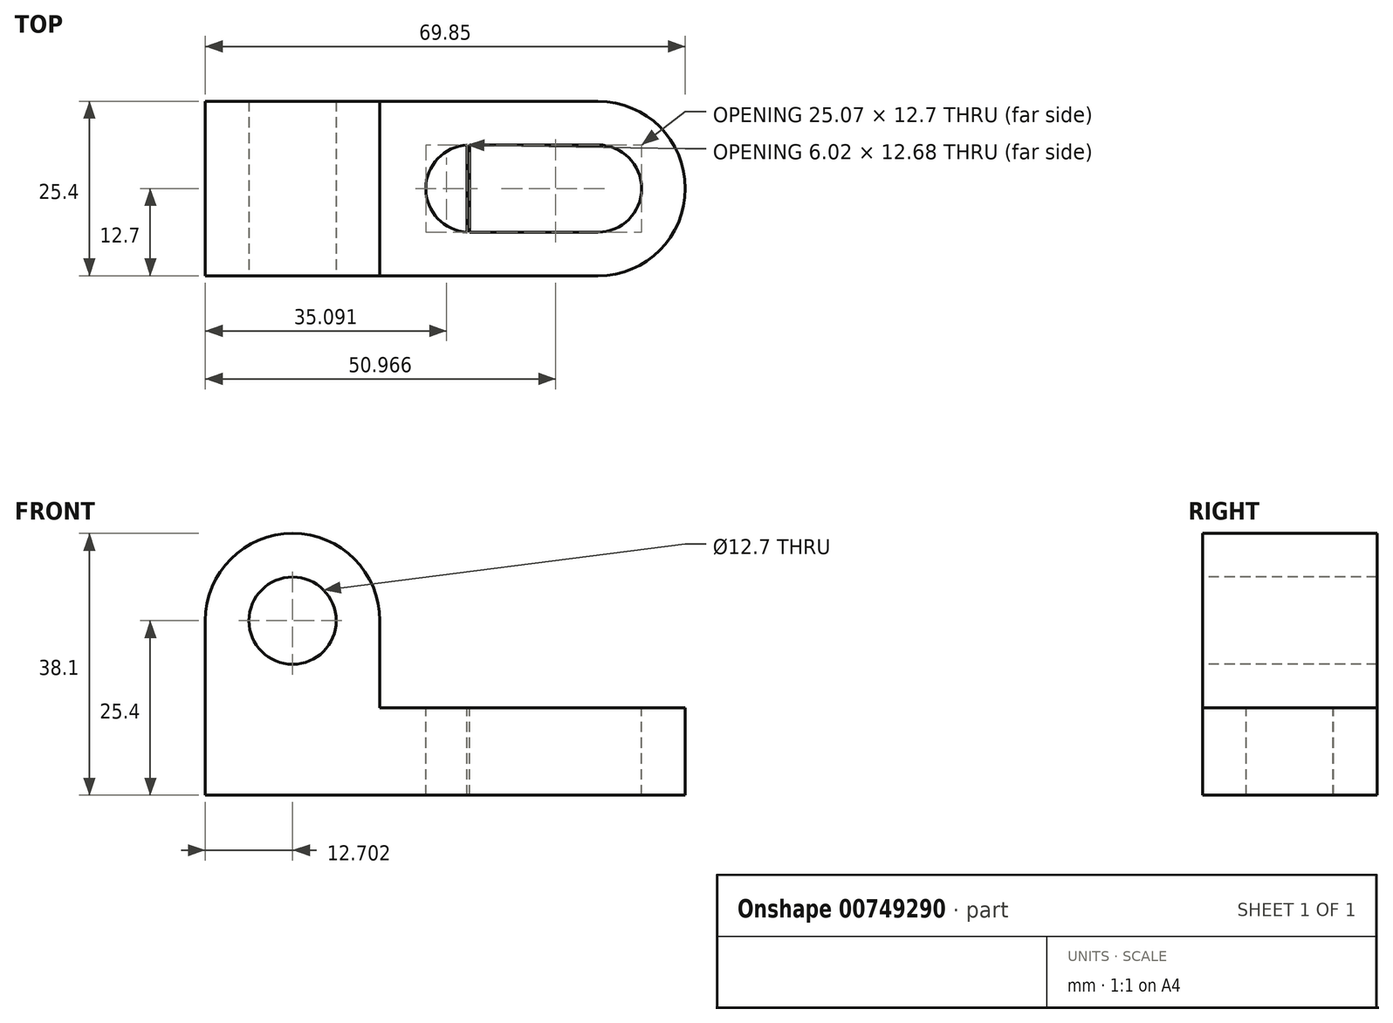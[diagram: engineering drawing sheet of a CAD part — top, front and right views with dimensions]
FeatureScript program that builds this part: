
annotation { "Feature Type Name" : "Feature", "Feature Type Description" : "" }
export const myFeature = defineFeature(function(context is Context, id is Id, definition is map)
    precondition{}
    {
        {
            var Q0;
            Q0=qCreatedBy(makeId("Front.planeOp"),FACE);
            var sketch = newSketch(context, id + "F0", { "sketchPlane" : qUnion([Q0])});
            skLineSegment(sketch, "E0", {"start": v(-38.43, 0) * mm, "end": v(-38.43, 38.1) * mm});
            skLineSegment(sketch, "E1", {"start": v(-38.43, 38.1) * mm, "end": v(-13.03, 38.1) * mm});
            skLineSegment(sketch, "E2", {"start": v(-13.03, 38.1) * mm, "end": v(-13.03, 12.7) * mm});
            skLineSegment(sketch, "E3", {"start": v(-13.03, 12.7) * mm, "end": v(31.42, 12.7) * mm});
            skLineSegment(sketch, "E4", {"start": v(31.42, 12.7) * mm, "end": v(31.42, 0) * mm});
            skLineSegment(sketch, "E5", {"start": v(31.42, 0) * mm, "end": v(-38.43, 0) * mm});
            skSolve(sketch);
        }
        {
            var Q0;
            Q0=makeQuery(id+"F0.imprint","IMPRINT",FACE,{"disambiguationData":[TD([[makeQuery(id+"F0.imprint","IMPRINT",EDGE,{"derivedFrom":sQuery(id+"F0.wireOp",EDGE,"E0")}),-1.0]])]});
            extrude(context, id + "F1", {"entities" : qUnion([Q0]), "depth" : 25.4 * mm, "offsetDistance" : 25.4 * mm});
        }
        {
            var Q0;
            Q0=makeQuery(id+"F1.opExtrude","CAP_FACE",FACE,{"disambiguationData":[OSD([sQuery(id+"F0.wireOp",EDGE,"E0"),sQuery(id+"F0.wireOp",EDGE,"E1"),sQuery(id+"F0.wireOp",EDGE,"E2"),sQuery(id+"F0.wireOp",EDGE,"E3"),sQuery(id+"F0.wireOp",EDGE,"E4"),sQuery(id+"F0.wireOp",EDGE,"E5")])],"isStart":false});
            var sketch = newSketch(context, id + "F2", { "sketchPlane" : qUnion([Q0])});
            skLineSegment(sketch, "E6", {"start": v(-38.43, 25.4) * mm, "end": v(-13.03, 25.4) * mm});
            skLineSegment(sketch, "E7", {"start": v(-13.03, 25.4) * mm, "end": v(-13.03, 38.1) * mm});
            skCircle(sketch, "E8", {"center": v(-25.73, 25.4) * mm, "radius": 6.35 * mm});
            skArc(sketch, "E9", {"start": v(-13.03, 25.4) * mm, "mid": v(-25.73, 38.1) * mm, "end": v(-38.43, 25.4) * mm});
            skSolve(sketch);
        }
        {
            var Q0;
            {var subQ1=makeQuery(id+"F1.opExtrude","CAP_EDGE",EDGE,{"disambiguationData":[OSD([sQuery(id+"F0.wireOp",EDGE,"E0")])],"isStart":false});var subQ3=makeQuery(id+"F1.opExtrude","CAP_EDGE",EDGE,{"disambiguationData":[OSD([sQuery(id+"F0.wireOp",EDGE,"E1")])],"isStart":false});var subQ5=makeQuery(id+"F2.imprint","INTERSECT",VERTEX,{"derivedFrom":[subQ1,subQ3]});Q0=makeQuery(id+"F2.imprint","IMPRINT",FACE,{"disambiguationData":[TD([[makeQuery(id+"F2.imprint","IMPRINT",EDGE,{"disambiguationData":[TD([[subQ5,-1.0]])],"derivedFrom":subQ3}),-1.0]])]});}
            var Q1;
            {var subQ0=sQuery(id+"F2.wireOp",EDGE,"E7");Q1=makeQuery(id+"F2.imprint","IMPRINT",FACE,{"disambiguationData":[TD([[makeQuery(id+"F2.imprint","IMPRINT",EDGE,{"derivedFrom":subQ0}),-1.0]])]});}
            var Q2;
            {var subQ0=sQuery(id+"F2.wireOp",EDGE,"E8");var subQ1=sQuery(id+"F2.wireOp",EDGE,"E6");var subQ2=makeQuery(id+"F2.imprint","INTERSECT",VERTEX,{"disambiguationData":[OD(0.0)],"derivedFrom":[subQ1,subQ0]});Q2=makeQuery(id+"F2.imprint","IMPRINT",FACE,{"disambiguationData":[TD([[makeQuery(id+"F2.imprint","IMPRINT",EDGE,{"disambiguationData":[TD([[subQ2,-1.0]])],"derivedFrom":subQ1}),1.0]])]});}
            var Q3;
            {var subQ0=sQuery(id+"F2.wireOp",EDGE,"E8");var subQ1=sQuery(id+"F2.wireOp",EDGE,"E6");var subQ2=makeQuery(id+"F2.imprint","INTERSECT",VERTEX,{"disambiguationData":[OD(0.0)],"derivedFrom":[subQ1,subQ0]});Q3=makeQuery(id+"F2.imprint","IMPRINT",FACE,{"disambiguationData":[TD([[makeQuery(id+"F2.imprint","IMPRINT",EDGE,{"disambiguationData":[TD([[subQ2,-1.0]])],"derivedFrom":subQ1}),-1.0]])]});}
            extrude(context, id + "F3", {"entities" : qUnion([Q0, Q1, Q2, Q3]), "operationType" : NewBodyOperationType.REMOVE, "endBound" : BoundingType.THROUGH_ALL, "oppositeDirection" : true, "depth" : 25.4 * mm, "offsetDistance" : 25.4 * mm});
        }
        {
            var Q0;
            Q0=makeQuery(id+"F1.opExtrude","SWEPT_FACE",FACE,{"disambiguationData":[OSD([sQuery(id+"F0.wireOp",EDGE,"E3")])]});
            var sketch = newSketch(context, id + "F4", { "sketchPlane" : qUnion([Q0])});
            skLineSegment(sketch, "E10", {"start": v(0, 0) * mm, "end": v(0, -25.4) * mm});
            skLineSegment(sketch, "E11", {"start": v(18.72, 0) * mm, "end": v(18.72, -25.4) * mm});
            skLineSegment(sketch, "E12", {"start": v(18.72, 0) * mm, "end": v(31.42, 0) * mm});
            skLineSegment(sketch, "E13", {"start": v(0, 0) * mm, "end": v(18.72, 0) * mm});
            skLineSegment(sketch, "E14", {"start": v(-0.33, 0) * mm, "end": v(-0.33, -25.4) * mm});
            skLineSegment(sketch, "E15", {"start": v(-0.33, -25.4) * mm, "end": v(18.72, -25.4) * mm});
            skCircle(sketch, "E16", {"center": v(0, -12.7) * mm, "radius": 6.35 * mm});
            skCircle(sketch, "E17", {"center": v(18.72, -12.7) * mm, "radius": 6.35 * mm});
            skLineSegment(sketch, "E18", {"start": v(0, -6.35) * mm, "end": v(18.72, -6.35) * mm});
            skLineSegment(sketch, "E19", {"start": v(18.72, -19.05) * mm, "end": v(0, -19.05) * mm});
            skArc(sketch, "E20", {"start": v(18.72, -25.4) * mm, "mid": v(31.42, -12.7) * mm, "end": v(18.72, 0) * mm});
            skSolve(sketch);
        }
        {
            var Q0;
            {var subQ0=sQuery(id+"F4.wireOp",EDGE,"E16");var subQ1=sQuery(id+"F4.wireOp",EDGE,"E10");var subQ2=makeQuery(id+"F4.imprint","INTERSECT",VERTEX,{"derivedFrom":[subQ1,subQ0,sQuery(id+"F4.wireOp",EDGE,"E18")]});Q0=makeQuery(id+"F4.imprint","IMPRINT",FACE,{"disambiguationData":[TD([[makeQuery(id+"F4.imprint","IMPRINT",EDGE,{"disambiguationData":[TD([[subQ2,-1.0]])],"derivedFrom":subQ1}),1.0]])]});}
            var Q1;
            {var subQ0=sQuery(id+"F4.wireOp",EDGE,"E16");var subQ1=sQuery(id+"F4.wireOp",EDGE,"E14");var subQ2=makeQuery(id+"F4.imprint","INTERSECT",VERTEX,{"disambiguationData":[OD(0.0)],"derivedFrom":[subQ1,subQ0]});Q1=makeQuery(id+"F4.imprint","IMPRINT",FACE,{"disambiguationData":[TD([[makeQuery(id+"F4.imprint","IMPRINT",EDGE,{"disambiguationData":[TD([[subQ2,-1.0]])],"derivedFrom":subQ1}),-1.0]])]});}
            var Q2;
            {var subQ0=sQuery(id+"F4.wireOp",EDGE,"E18");Q2=makeQuery(id+"F4.imprint","IMPRINT",FACE,{"disambiguationData":[TD([[makeQuery(id+"F4.imprint","IMPRINT",EDGE,{"derivedFrom":subQ0}),-1.0]])]});}
            var Q3;
            {var subQ0=sQuery(id+"F4.wireOp",EDGE,"E17");var subQ1=sQuery(id+"F4.wireOp",EDGE,"E11");var subQ2=makeQuery(id+"F4.imprint","INTERSECT",VERTEX,{"derivedFrom":[subQ1,subQ0,sQuery(id+"F4.wireOp",EDGE,"E18")]});Q3=makeQuery(id+"F4.imprint","IMPRINT",FACE,{"disambiguationData":[TD([[makeQuery(id+"F4.imprint","IMPRINT",EDGE,{"disambiguationData":[TD([[subQ2,-1.0]])],"derivedFrom":subQ1}),-1.0]])]});}
            var Q4;
            {var subQ0=sQuery(id+"F4.wireOp",EDGE,"E17");var subQ1=sQuery(id+"F4.wireOp",EDGE,"E11");var subQ2=makeQuery(id+"F4.imprint","INTERSECT",VERTEX,{"derivedFrom":[subQ1,subQ0,sQuery(id+"F4.wireOp",EDGE,"E18")]});Q4=makeQuery(id+"F4.imprint","IMPRINT",FACE,{"disambiguationData":[TD([[makeQuery(id+"F4.imprint","IMPRINT",EDGE,{"disambiguationData":[TD([[subQ2,-1.0]])],"derivedFrom":subQ1}),1.0]])]});}
            var Q5;
            {var subQ0=sQuery(id+"F4.wireOp",EDGE,"E12");Q5=makeQuery(id+"F4.imprint","IMPRINT",FACE,{"disambiguationData":[TD([[makeQuery(id+"F4.imprint","IMPRINT",EDGE,{"derivedFrom":subQ0}),-1.0]])]});}
            var Q6;
            {var subQ0=sQuery(id+"F4.wireOp",EDGE,"E20");var subQ1=sQuery(id+"F0.wireOp",EDGE,"E3");var subQ4=makeQuery(id+"F1.opExtrude","SWEPT_EDGE",EDGE,{"disambiguationData":[OSD([subQ1,sQuery(id+"F0.wireOp",EDGE,"E4")])]});var subQ5=makeQuery(id+"F4.imprint","INTERSECT",VERTEX,{"derivedFrom":[subQ4,subQ0]});Q6=makeQuery(id+"F4.imprint","IMPRINT",FACE,{"disambiguationData":[TD([[makeQuery(id+"F4.imprint","IMPRINT",EDGE,{"disambiguationData":[TD([[subQ5,1.0]])],"derivedFrom":subQ0}),-1.0]])]});}
            extrude(context, id + "F5", {"entities" : qUnion([Q0, Q1, Q2, Q3, Q4, Q5, Q6]), "operationType" : NewBodyOperationType.REMOVE, "endBound" : BoundingType.THROUGH_ALL, "oppositeDirection" : true, "depth" : 25.4 * mm, "offsetDistance" : 25.4 * mm});
        }
    });
